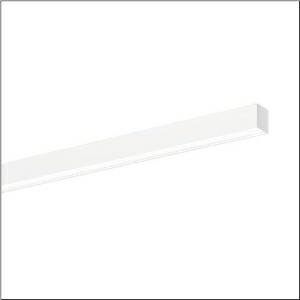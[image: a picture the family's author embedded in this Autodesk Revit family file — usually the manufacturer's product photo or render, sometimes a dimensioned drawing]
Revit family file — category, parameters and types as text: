
# Revit family: silica_21_51mx20dc45wb
name_source: partatom
category: Lighting Fixtures
units: mm (PartAtom-declared; Revit-internal decimal feet)

## family parameters
Cut with Voids When Loaded = No
Host = Face
Light Source = No
Part Type = Normal
Room Calculation Point = No
Round Connector Dimension = Use Diameter
Shared = No

## types (1)
- --- (1 x LED, 6000 lm, 40.1 W, 4000K)
    Apparent Load = 40 VA
    CIE Flux Codes = 48 79 96 100 100
    Color Rendering = 80
    Color Temperature = 4000K
    Default Elevation = 1800 mm
    Description = Silica 21, office luminaire, primary optical cover: cover, of PMMA, opal, light emission: direct distribution, primary light characteristic: symmetric, installation type: surface-mounted, LED, rated luminous flux: 6.000lm, luminous efficacy: 150lm/W, light colour: 840, colour temperature: 4000K, control gear: DALI 2, with terminal, 3+2-pole, max. 2.5mm², mains connection: 220..240V, AC, 50/60Hz, rated input power: 40.1W, luminaire housing, of aluminium, traffic white (RAL 9016), length: 3.004mm, width: 53mm, height: 53mm, protection rating (complete): IP20, insulation class (complete): insulation class I (protective earthing), certification: CE, permissible operating ambient temperature: 0..+35°C, standard: EN 50419, packaging unit: 1 piece
    Height = 53 mm
    Lamp = 1 x LED
    Lamp Light Flux = 6000 lm
    Lamp Power = 40.1 W
    Lamp count = 1
    Length = 3004 mm
    Luminous efficacy = 150 lm/W
    Manufacturer = Siteco
    ModVariant = No
    Model = 51MX20DC45WB
    Mounting Place = Ceiling
    Mounting Type = Surface mounted
    Number of Poles = 1
    OnlyDefault = Yes
    Power Factor = 1
    Product Name = Silica 21
    Product group = office luminaire | ceiling mounted
    ProductGroupID = 301
    Protection Class = Protection class I
    Protection Degree = IP 20
    RLX_Detail_Level = 1
    RLX_Emergency_Light_Flux = 0 lm
    RLX_Emergency_Type = 0
    RLX_Emergency_Type_DB = No
    RlxData = <blob elided: 23841 chars, md5=d79dea3f>
    Socket = socket
    Standby Power = 0 W
    System Light Flux = 6000 lm
    System Power = 40 W
    Type Comments = factory setting: luminous flux: 100 % | dim-lin: 254 | 218 mA
    Type Image = l_1335877.jpg
    URL = http://relux.com
    VarID = @adj_118053
    Voltage = 0 V
    Weight = 0.00 kg
    Width = 53 mm

## geometry (parser evidence)
native form markers: Blend x4, Sweep x10
no freeform markers — native parametric forms only
